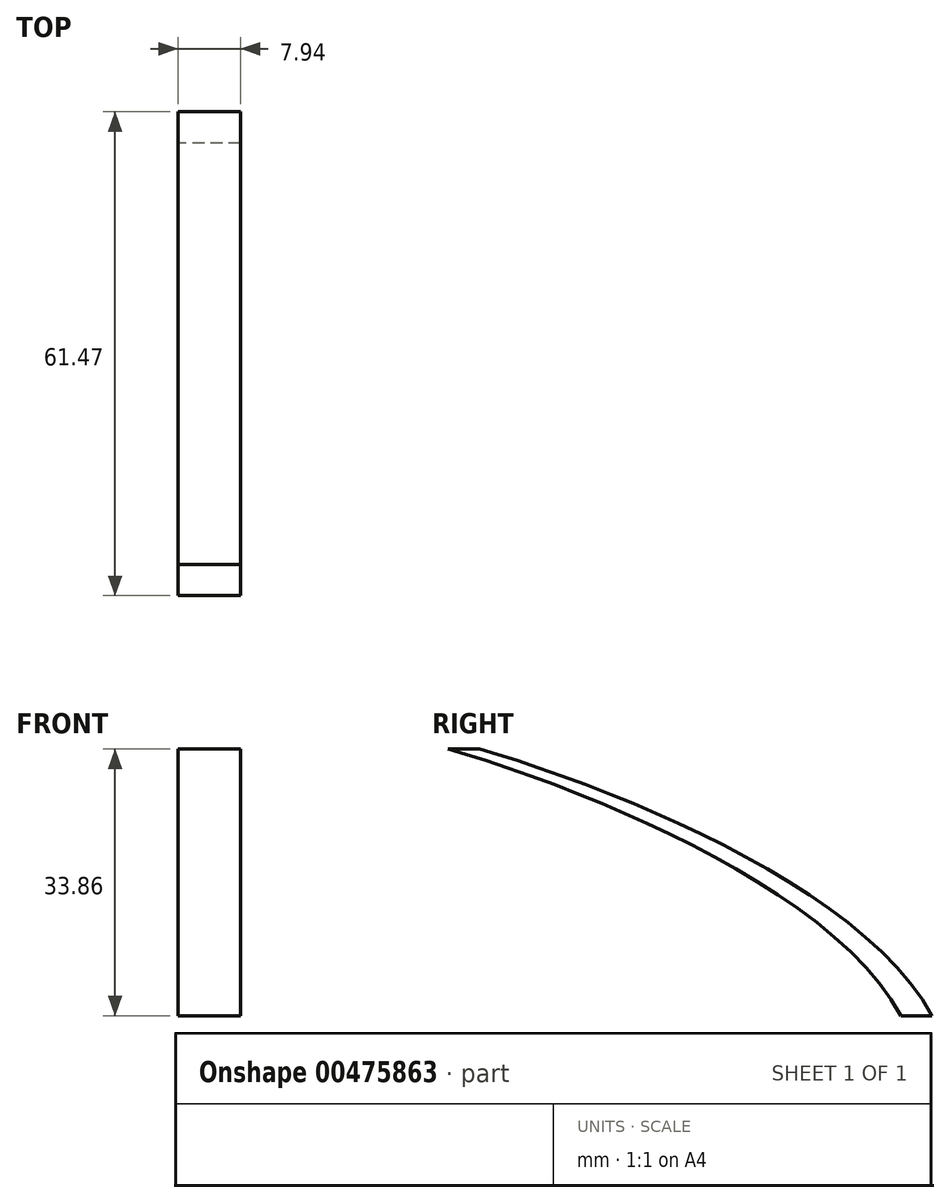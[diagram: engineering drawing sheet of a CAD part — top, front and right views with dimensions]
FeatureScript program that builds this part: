
annotation { "Feature Type Name" : "Feature", "Feature Type Description" : "" }
export const myFeature = defineFeature(function(context is Context, id is Id, definition is map)
    precondition{}
    {
        {
            var Q0;
            Q0=qCreatedBy(makeId("Front.planeOp"),FACE);
            var sketch = newSketch(context, id + "F0", { "sketchPlane" : qUnion([Q0])});
            skLineSegment(sketch, "E0", {"start": v(209.38, -129.63) * mm, "end": v(266.53, -129.63) * mm});
            skFitSpline(sketch, "E1", {"points": [v(-423.46, 276.77) * mm, v(266.53, -129.63) * mm], "startDerivative": vector(266.7, -304.8) * mm, "endDerivative": vector(325.52, -609.6) * mm});
            skPoint(sketch, "E2.endSnap0", {"position": v(-51.73, -54.47) * mm});
            skLineSegment(sketch, "E3", {"start": v(158.03, 73.57) * mm, "end": v(153.17, -158.97) * mm});
            skFitSpline(sketch, "E4", {"points": [v(-423.46, 276.77) * mm, v(266.53, -129.63) * mm], "startDerivative": vector(533.4, -152.4) * mm, "endDerivative": vector(325.52, -609.6) * mm});
            skLineSegment(sketch, "E5", {"start": v(266.53, -129.63) * mm, "end": v(266.53, 22.77) * mm});
            skLineSegment(sketch, "E6", {"start": v(266.53, 22.77) * mm, "end": v(158.03, 25.04) * mm});
            skLineSegment(sketch, "E7", {"start": v(266.53, -129.63) * mm, "end": v(266.53, 73.57) * mm});
            skLineSegment(sketch, "E8", {"start": v(266.53, 73.57) * mm, "end": v(158.03, 73.57) * mm});
            skSolve(sketch);
        }
        {
            var Q0;
            Q0=qCreatedBy(makeId("Top.planeOp"),FACE);
            var sketch = newSketch(context, id + "F1", { "sketchPlane" : qUnion([Q0])});
            skLineSegment(sketch, "E9.bottom", {"start": v(28.58, -38.1) * mm, "end": v(-19.05, -38.1) * mm});
            skLineSegment(sketch, "E9.top", {"start": v(28.57, 57.15) * mm, "end": v(-19.05, 57.15) * mm});
            skLineSegment(sketch, "E9.left", {"start": v(28.58, -38.1) * mm, "end": v(28.58, 57.15) * mm});
            skLineSegment(sketch, "E9.right", {"start": v(-19.05, -38.1) * mm, "end": v(-19.05, 57.15) * mm});
            skPoint(sketch, "E9.middle", {"position": v(4.76, 9.53) * mm});
            skSolve(sketch);
        }
        {
            var Q0;
            Q0=makeQuery(id+"F1.imprint","IMPRINT",FACE,{"disambiguationData":[TD([[makeQuery(id+"F1.imprint","IMPRINT",EDGE,{"derivedFrom":sQuery(id+"F1.wireOp",EDGE,"E9.bottom")}),-1.0]])]});
            extrude(context, id + "F2", {"entities" : qUnion([Q0]), "depth" : 203.2 * mm, "offsetDistance" : 25.4 * mm});
        }
        {
            var Q0;
            Q0=makeQuery(id+"F2.opExtrude","CAP_FACE",FACE,{"disambiguationData":[OSD([sQuery(id+"F1.wireOp",EDGE,"E9.bottom"),sQuery(id+"F1.wireOp",EDGE,"E9.top"),sQuery(id+"F1.wireOp",EDGE,"E9.left"),sQuery(id+"F1.wireOp",EDGE,"E9.right")])],"isStart":false});
            var Q1;
            Q1=sQuery(id+"F0.wireOp",EDGE,"E4");
            sweep(context, id + "F3", {"profiles" : qUnion([Q0]), "path" : qUnion([Q1]), "keepProfileOrientation" : true});
        }
        {
            var Q0;
            Q0=makeQuery(id+"F2.opExtrude","SWEPT_BODY",BODY,{"disambiguationData":[OSD([sQuery(id+"F1.wireOp",EDGE,"E9.bottom"),sQuery(id+"F1.wireOp",EDGE,"E9.top"),sQuery(id+"F1.wireOp",EDGE,"E9.left"),sQuery(id+"F1.wireOp",EDGE,"E9.right")])]});
            deleteBodies(context, id + "F4", {"entities" : qUnion([Q0])});
        }
        {
            var Q0;
            Q0=qCreatedBy(makeId("Front.planeOp"),FACE);
            var sketch = newSketch(context, id + "F5", { "sketchPlane" : qUnion([Q0])});
            skLineSegment(sketch, "E10", {"start": v(0, 0) * mm, "end": v(0, 73) * mm});
            skSolve(sketch);
        }
        {
            var Q0;
            Q0=makeQuery(id+"F3.opSweep","SWEPT_BODY",BODY,{"disambiguationData":[OSD([sQuery(id+"F0.wireOp",EDGE,"E4"),sQuery(id+"F1.wireOp",EDGE,"E9.bottom"),sQuery(id+"F1.wireOp",EDGE,"E9.top"),sQuery(id+"F1.wireOp",EDGE,"E9.left"),sQuery(id+"F1.wireOp",EDGE,"E9.right")])]});
            var Q1;
            Q1=sQuery(id+"F5.wireOp",EDGE,"E10");
            transform(context, id + "F6", {"entities" : qUnion([Q0]), "transformType" : TransformType.ROTATION, "transformAxis" : qUnion([Q1]), "angle" : 90 * degree, "makeCopy" : false});
        }
        {
            var Q0;
            Q0=makeQuery(id+"F3.opSweep","SWEPT_BODY",BODY,{"disambiguationData":[OSD([sQuery(id+"F0.wireOp",EDGE,"E4"),sQuery(id+"F1.wireOp",EDGE,"E9.bottom"),sQuery(id+"F1.wireOp",EDGE,"E9.top"),sQuery(id+"F1.wireOp",EDGE,"E9.left"),sQuery(id+"F1.wireOp",EDGE,"E9.right")])]});
            var Q1;
            Q1=qCreatedBy(makeId("Origin.pointOp"),VERTEX);
            transform(context, id + "F7", {"entities" : qUnion([Q0]), "transformType" : TransformType.SCALE_UNIFORMLY, "scale" : 1 / 12, "scalePoint" : qUnion([Q1]), "makeCopy" : false});
        }
    });
